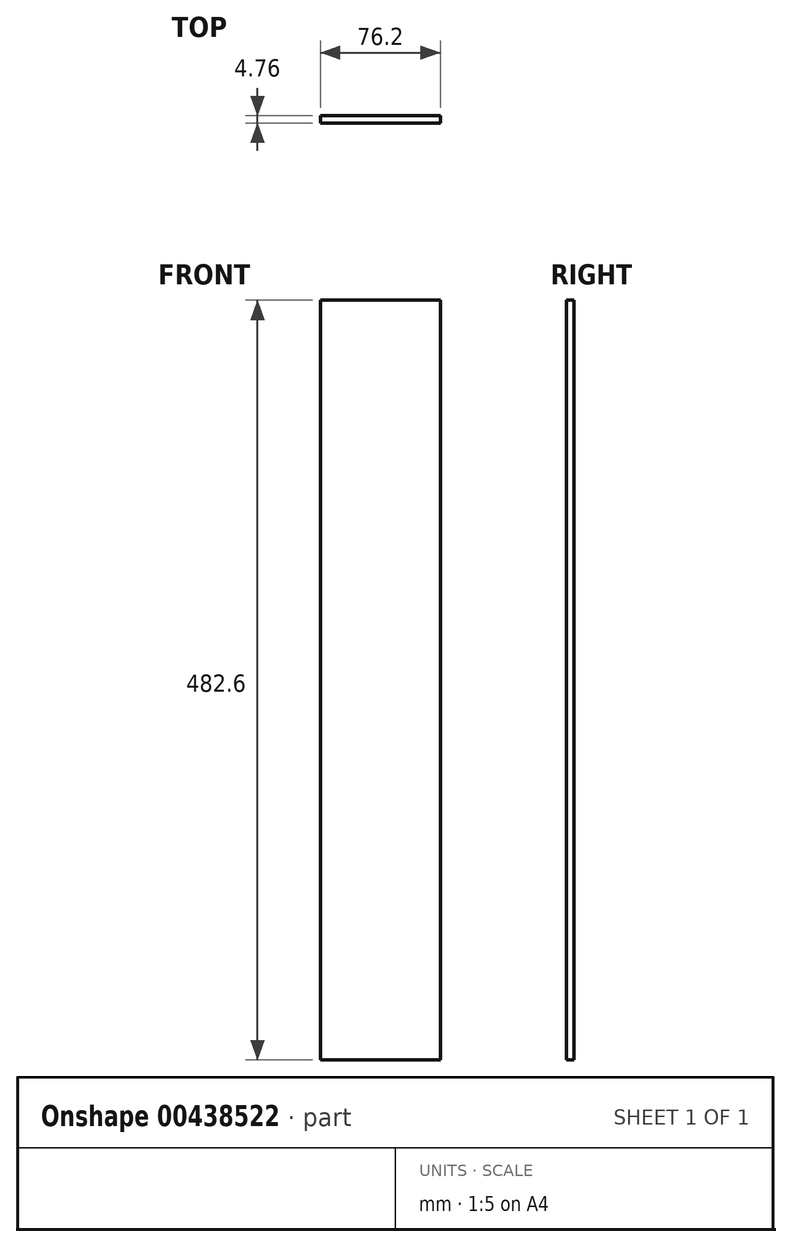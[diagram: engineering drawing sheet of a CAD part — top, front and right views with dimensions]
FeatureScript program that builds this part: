
annotation { "Feature Type Name" : "Feature", "Feature Type Description" : "" }
export const myFeature = defineFeature(function(context is Context, id is Id, definition is map)
    precondition{}
    {
        {
            var Q0;
            Q0=qCreatedBy(makeId("Front.planeOp"),FACE);
            var sketch = newSketch(context, id + "F0", { "sketchPlane" : qUnion([Q0])});
            skLineSegment(sketch, "E0.bottom", {"start": v(-25.1, 432.9) * mm, "end": v(51.1, 432.9) * mm});
            skLineSegment(sketch, "E0.top", {"start": v(-25.1, -49.7) * mm, "end": v(51.1, -49.7) * mm});
            skLineSegment(sketch, "E0.left", {"start": v(-25.1, 432.9) * mm, "end": v(-25.1, -49.7) * mm});
            skLineSegment(sketch, "E0.right", {"start": v(51.1, 432.9) * mm, "end": v(51.1, -49.7) * mm});
            skSolve(sketch);
        }
        {
            var Q0;
            Q0=makeQuery(id+"F0.imprint","IMPRINT",FACE,{"disambiguationData":[TD([[makeQuery(id+"F0.imprint","IMPRINT",EDGE,{"derivedFrom":sQuery(id+"F0.wireOp",EDGE,"E0.bottom")}),-1.0]])]});
            extrude(context, id + "F1", {"entities" : qUnion([Q0]), "depth" : 4.76 * mm});
        }
    });
